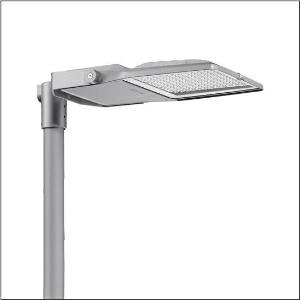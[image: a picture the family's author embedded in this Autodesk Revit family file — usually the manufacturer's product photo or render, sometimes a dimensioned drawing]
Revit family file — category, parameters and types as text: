
# Revit family: floodlight_fl_21_iq_midi___pl43_5xa7782e4a3a_f2c8
name_source: partatom
category: Lighting Fixtures
units: mm (PartAtom-declared; Revit-internal decimal feet)

## family parameters
Cut with Voids When Loaded = No
Host = Face
Light Source = No
Part Type = Normal
Room Calculation Point = No
Round Connector Dimension = Use Diameter
Shared = No

## types (1)
- --- (1 x LED, 28730 lm, 208.1 W, 4000K)
    Apparent Load = 208 VA
    CIE Flux Codes = 27 78 99 100 100
    Color Rendering = 70
    Color Temperature = 4000K
    Default Elevation = 1800 mm
    Description = Floodlight FL 21 iQ midi, floodlight, primary light control with lens, of PMMA, primary optical cover: protective disc, of toughened safety glass, transparent, light distribution: PL43, light emission: direct distribution, installation type: surface-mounted, LED, High Power LED, rated luminous flux: 28.730lm, luminous efficacy: 138lm/W, light colour: 740, colour temperature: 4000K, control gear: ECG iQ, control: optimised constant luminous flux control (CLO 2.0), Desk-Remote (wireless, voltage-free reading and setting of iQ features in the workshop via application-optimized NFC function/RFID function), Smart-Wire, Night-Set, Temp-Guard, Auto-Match, Street-Remote, with terminal, 6-pole, mains connection: 220..240V, AC, 50/60Hz, start of lifetime: 208W, end of service life: 227W, reduction: 90W, luminaire housing, of diecast aluminium, powder-coated, Siteco® metallic grey (DB 702S), corrosivity category C5 mid according to DIN EN ISO 12944, sealing non-destructively replaceable, please order mast flange separately, mast bracket, of steel, galvanised, powder-coated, Siteco® metallic grey (DB 702S), protection rating (complete): IP66, insulation class (complete): insulation class II (safety insulation), certification: CE, protection symbol: D, impact resistance: IK08, permissible operating ambient temperature: -40..+40°C, permissible operating ambient temperature for outdoor applications: -40..+50°C, standard: DIN EN 12944, LABS conformity tested according to VDMA 24364:2018-05, packaging unit: 1 piece

Light Distribution: PL43
    Height = 76 mm
    Lamp = 1 x LED
    Lamp Light Flux = 28730 lm
    Lamp Power = 208.1 W
    Lamp count = 1
    Length = 657 mm
    Luminous efficacy = 138 lm/W
    Manufacturer = Siteco
    ModVariant = No
    Model = 5XA7782E4A3A
    Number of Poles = 1
    OnlyDefault = Yes
    Power Factor = 1
    Product Name = Floodlight FL 21 iQ midi | PL43
    Product group = floodlight | pylon annexe
    ProductGroupID = 6200
    Protection Class = Protection class II
    Protection Degree = IP 66
    RLX_Detail_Level = 1
    RLX_Emergency_Light_Flux = 0 lm
    RLX_Emergency_Type = 0
    RLX_Emergency_Type_DB = No
    RlxData = <blob elided: 153429 chars, md5=8c59862d>
    Socket = socket
    Standby Power = 0 W
    System Light Flux = 28730 lm
    System Power = 208 W
    Type Comments = factory setting: luminous flux: 100 % | dim-lin: 254 | 710 mA
    Type Image = l_1007123.jpg
    URL = http://relux.com
    VarID = @adj_053357
    Voltage = 0 V
    Weight = 0.00 kg
    Width = 442 mm

## geometry (parser evidence)
native form markers: Blend x4, Sweep x13
no freeform markers — native parametric forms only
